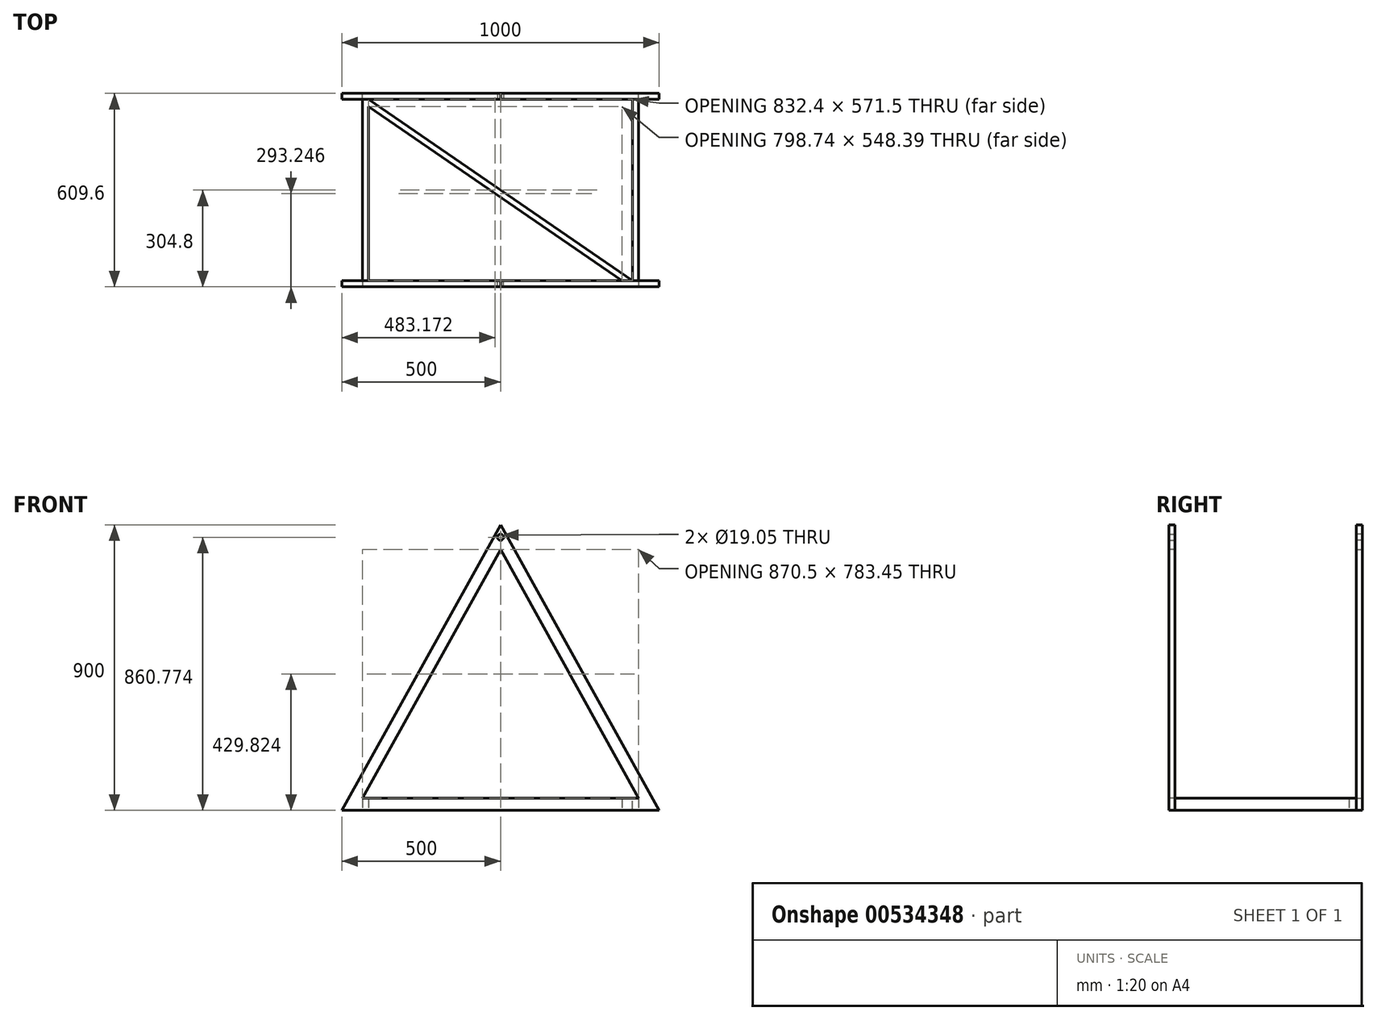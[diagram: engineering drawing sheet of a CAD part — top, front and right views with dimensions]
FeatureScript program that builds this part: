
annotation { "Feature Type Name" : "Feature", "Feature Type Description" : "" }
export const myFeature = defineFeature(function(context is Context, id is Id, definition is map)
    precondition{}
    {
        {
            var Q0;
            Q0=qCreatedBy(makeId("Front.planeOp"),FACE);
            var sketch = newSketch(context, id + "F0", { "sketchPlane" : qUnion([Q0])});
            skLineSegment(sketch, "E0", {"start": v(0, 900) * mm, "end": v(-500, 0) * mm});
            skLineSegment(sketch, "E1", {"start": v(-500, 0) * mm, "end": v(500, 0) * mm});
            skLineSegment(sketch, "E2", {"start": v(500, 0) * mm, "end": v(0, 900) * mm});
            skLineSegment(sketch, "E3", {"start": v(0, 900) * mm, "end": v(0, 0) * mm, "construction": true});
            skLineSegment(sketch, "E4", {"start": v(-478.83, 38.1) * mm, "end": v(478.83, 38.1) * mm});
            skLineSegment(sketch, "E5", {"start": v(-21.8, 860.77) * mm, "end": v(456.42, 0) * mm});
            skLineSegment(sketch, "E6", {"start": v(21.8, 860.77) * mm, "end": v(-456.42, 0) * mm});
            skSolve(sketch);
        }
        {
            var Q0;
            {var subQ0=sQuery(id+"F0.wireOp",EDGE,"E5");var subQ1=sQuery(id+"F0.wireOp",EDGE,"E1");var subQ2=makeQuery(id+"F0.imprint","INTERSECT",VERTEX,{"derivedFrom":[subQ1,subQ0]});Q0=makeQuery(id+"F0.imprint","IMPRINT",FACE,{"disambiguationData":[TD([[makeQuery(id+"F0.imprint","IMPRINT",EDGE,{"disambiguationData":[TD([[subQ2,1.0]])],"derivedFrom":subQ1}),1.0]])]});}
            extrude(context, id + "F1", {"entities" : qUnion([Q0]), "depth" : 19.05 * mm, "offsetDistance" : 25 * mm});
        }
        {
            var Q0;
            {var subQ0=sQuery(id+"F0.wireOp",EDGE,"E2");var subQ1=sQuery(id+"F0.wireOp",EDGE,"E1");var subQ2=makeQuery(id+"F0.imprint","INTERSECT",VERTEX,{"derivedFrom":[subQ1,subQ0]});Q0=makeQuery(id+"F0.imprint","IMPRINT",FACE,{"disambiguationData":[TD([[makeQuery(id+"F0.imprint","IMPRINT",EDGE,{"disambiguationData":[TD([[subQ2,1.0]])],"derivedFrom":subQ1}),1.0]])]});}
            var Q1;
            {var subQ0=sQuery(id+"F0.wireOp",EDGE,"E4");var subQ1=sQuery(id+"F0.wireOp",EDGE,"E2");var subQ2=makeQuery(id+"F0.imprint","INTERSECT",VERTEX,{"derivedFrom":[subQ1,subQ0]});Q1=makeQuery(id+"F0.imprint","IMPRINT",FACE,{"disambiguationData":[TD([[makeQuery(id+"F0.imprint","IMPRINT",EDGE,{"disambiguationData":[TD([[subQ2,-1.0]])],"derivedFrom":subQ1}),1.0]])]});}
            var Q2;
            {var subQ0=sQuery(id+"F0.wireOp",EDGE,"E2");var subQ1=sQuery(id+"F0.wireOp",EDGE,"E0");var subQ2=makeQuery(id+"F0.imprint","INTERSECT",VERTEX,{"derivedFrom":[subQ1,subQ0]});Q2=makeQuery(id+"F0.imprint","IMPRINT",FACE,{"disambiguationData":[TD([[makeQuery(id+"F0.imprint","IMPRINT",EDGE,{"disambiguationData":[TD([[subQ2,-1.0]])],"derivedFrom":subQ1}),1.0]])]});}
            var Q3;
            {var subQ0=sQuery(id+"F0.wireOp",EDGE,"E4");var subQ1=sQuery(id+"F0.wireOp",EDGE,"E0");var subQ2=makeQuery(id+"F0.imprint","INTERSECT",VERTEX,{"derivedFrom":[subQ1,subQ0]});Q3=makeQuery(id+"F0.imprint","IMPRINT",FACE,{"disambiguationData":[TD([[makeQuery(id+"F0.imprint","IMPRINT",EDGE,{"disambiguationData":[TD([[subQ2,1.0]])],"derivedFrom":subQ1}),1.0]])]});}
            var Q4;
            {var subQ0=sQuery(id+"F0.wireOp",EDGE,"E1");var subQ1=sQuery(id+"F0.wireOp",EDGE,"E0");var subQ2=makeQuery(id+"F0.imprint","INTERSECT",VERTEX,{"derivedFrom":[subQ1,subQ0]});Q4=makeQuery(id+"F0.imprint","IMPRINT",FACE,{"disambiguationData":[TD([[makeQuery(id+"F0.imprint","IMPRINT",EDGE,{"disambiguationData":[TD([[subQ2,1.0]])],"derivedFrom":subQ1}),1.0]])]});}
            extrude(context, id + "F2", {"entities" : qUnion([Q0, Q1, Q2, Q3, Q4]), "operationType" : NewBodyOperationType.ADD, "depth" : 19.05 * mm, "offsetDistance" : 25 * mm});
        }
        {
            var Q0;
            {var subQ0=sQuery(id+"F0.wireOp",EDGE,"E6");var subQ1=sQuery(id+"F0.wireOp",EDGE,"E5");var subQ2=sQuery(id+"F0.wireOp",EDGE,"E1");Q0=makeQuery(id+"F2.boolean.opBoolean","MERGE",FACE,{"derivedFrom":[makeQuery(id+"F1.opExtrude","CAP_FACE",FACE,{"disambiguationData":[OSD([subQ2,sQuery(id+"F0.wireOp",EDGE,"E4"),subQ1,subQ0])],"isStart":false}),makeQuery(id+"F2.opExtrude","CAP_FACE",FACE,{"disambiguationData":[OSD([sQuery(id+"F0.wireOp",EDGE,"E0"),subQ2,sQuery(id+"F0.wireOp",EDGE,"E2"),subQ1,subQ0])],"isStart":false})]});}
            var sketch = newSketch(context, id + "F3", { "sketchPlane" : qUnion([Q0])});
            skLineSegment(sketch, "E7", {"start": v(0, 900) * mm, "end": v(0, 821.55) * mm, "construction": true});
            skCircle(sketch, "E8", {"center": v(0, 860.77) * mm, "radius": 9.53 * mm});
            skSolve(sketch);
        }
        {
            var Q0;
            Q0=makeQuery(id+"F3.imprint","IMPRINT",FACE,{"disambiguationData":[TD([[makeQuery(id+"F3.imprint","IMPRINT",EDGE,{"derivedFrom":sQuery(id+"F3.wireOp",EDGE,"E8")}),1.0]])]});
            extrude(context, id + "F4", {"entities" : qUnion([Q0]), "operationType" : NewBodyOperationType.REMOVE, "oppositeDirection" : true, "depth" : 25 * mm, "offsetDistance" : 25 * mm});
        }
        {
            var Q0;
            {var subQ0=sQuery(id+"F0.wireOp",EDGE,"E6");var subQ1=sQuery(id+"F0.wireOp",EDGE,"E5");var subQ2=sQuery(id+"F0.wireOp",EDGE,"E1");Q0=makeQuery(id+"F2.boolean.opBoolean","MERGE",FACE,{"derivedFrom":[makeQuery(id+"F1.opExtrude","CAP_FACE",FACE,{"disambiguationData":[OSD([subQ2,sQuery(id+"F0.wireOp",EDGE,"E4"),subQ1,subQ0])],"isStart":false}),makeQuery(id+"F2.opExtrude","CAP_FACE",FACE,{"disambiguationData":[OSD([sQuery(id+"F0.wireOp",EDGE,"E0"),subQ2,sQuery(id+"F0.wireOp",EDGE,"E2"),subQ1,subQ0])],"isStart":false})]});}
            var sketch = newSketch(context, id + "F5", { "sketchPlane" : qUnion([Q0])});
            skLineSegment(sketch, "E9", {"start": v(-435.25, 38.1) * mm, "end": v(-435.25, 0) * mm});
            skLineSegment(sketch, "E10", {"start": v(-435.25, 0) * mm, "end": v(-416.2, 0) * mm});
            skLineSegment(sketch, "E11", {"start": v(-416.2, 0) * mm, "end": v(-416.2, 38.1) * mm});
            skLineSegment(sketch, "E12", {"start": v(-416.2, 38.1) * mm, "end": v(-435.25, 38.1) * mm});
            skLineSegment(sketch, "E13", {"start": v(435.25, 38.1) * mm, "end": v(435.25, 0) * mm});
            skLineSegment(sketch, "E14", {"start": v(435.25, 0) * mm, "end": v(416.2, 0) * mm});
            skLineSegment(sketch, "E15", {"start": v(416.2, 0) * mm, "end": v(416.2, 38.1) * mm});
            skLineSegment(sketch, "E16", {"start": v(416.2, 38.1) * mm, "end": v(435.25, 38.1) * mm});
            skSolve(sketch);
        }
        {
            var Q0;
            Q0=makeQuery(id+"F5.imprint","IMPRINT",FACE,{"disambiguationData":[TD([[makeQuery(id+"F5.imprint","IMPRINT",EDGE,{"derivedFrom":sQuery(id+"F5.wireOp",EDGE,"fFyfrfPh-Eq2j-K1ku-OToW-O3K3zpw26YUa")}),1.0]])]});
            var Q1;
            Q1=makeQuery(id+"F5.imprint","IMPRINT",FACE,{"disambiguationData":[TD([[makeQuery(id+"F5.imprint","IMPRINT",EDGE,{"derivedFrom":sQuery(id+"F5.wireOp",EDGE,"udyJFOjD-FLFl-QIxw-vqOu-JMlUizLs7YAt")}),-1.0]])]});
            var Q2;
            Q2=makeQuery(id+"F5.imprint","IMPRINT",FACE,{"disambiguationData":[TD([[makeQuery(id+"F5.imprint","IMPRINT",EDGE,{"derivedFrom":sQuery(id+"F5.wireOp",EDGE,"E9")}),1.0]])]});
            var Q3;
            Q3=makeQuery(id+"F5.imprint","IMPRINT",FACE,{"disambiguationData":[TD([[makeQuery(id+"F5.imprint","IMPRINT",EDGE,{"derivedFrom":sQuery(id+"F5.wireOp",EDGE,"E13")}),-1.0]])]});
            extrude(context, id + "F6", {"entities" : qUnion([Q0, Q1, Q2, Q3]), "operationType" : NewBodyOperationType.ADD, "depth" : (609.6 / 2 - 19.05) * mm, "offsetDistance" : 25 * mm});
        }
        {
            var Q0;
            Q0=makeQuery(id+"F1.opExtrude","SWEPT_BODY",BODY,{"disambiguationData":[OSD([sQuery(id+"F0.wireOp",EDGE,"E1"),sQuery(id+"F0.wireOp",EDGE,"E4"),sQuery(id+"F0.wireOp",EDGE,"E5"),sQuery(id+"F0.wireOp",EDGE,"E6")])]});
            var Q1;
            Q1=makeQuery(id+"F6.opExtrude","CAP_FACE",FACE,{"disambiguationData":[OSD([sQuery(id+"F5.wireOp",EDGE,"E13"),sQuery(id+"F5.wireOp",EDGE,"E14"),sQuery(id+"F5.wireOp",EDGE,"E15"),sQuery(id+"F5.wireOp",EDGE,"E16")])],"isStart":false});
            mirror(context, id + "F7", {"operationType" : NewBodyOperationType.ADD, "entities" : qUnion([Q0]), "mirrorPlane" : qUnion([Q1])});
        }
        {
            var Q0;
            Q0=qCreatedBy(makeId("Top.planeOp"),FACE);
            var sketch = newSketch(context, id + "F8", { "sketchPlane" : qUnion([Q0])});
            skLineSegment(sketch, "E17", {"start": v(-416.2, -19.05) * mm, "end": v(-416.2, -42.16) * mm});
            skLineSegment(sketch, "E18", {"start": v(-416.2, -42.16) * mm, "end": v(382.54, -590.55) * mm});
            skLineSegment(sketch, "E19", {"start": v(382.54, -590.55) * mm, "end": v(416.2, -590.55) * mm});
            skLineSegment(sketch, "E20", {"start": v(416.2, -590.55) * mm, "end": v(-416.2, -19.05) * mm});
            skLineSegment(sketch, "E21.0", {"start": v(-416.2, -590.55) * mm, "end": v(416.2, -590.55) * mm, "construction": true});
            skLineSegment(sketch, "E21.1", {"start": v(-416.2, -19.05) * mm, "end": v(416.2, -19.05) * mm, "construction": true});
            skSolve(sketch);
        }
        {
            var Q0;
            Q0=makeQuery(id+"F8.imprint","IMPRINT",FACE,{"disambiguationData":[TD([[makeQuery(id+"F8.imprint","IMPRINT",EDGE,{"derivedFrom":sQuery(id+"F8.wireOp",EDGE,"E17")}),1.0]])]});
            var Q1;
            {var subQ0=makeQuery(id+"F6.boolean.opBoolean","MERGE",FACE,{"derivedFrom":[makeQuery(id+"F1.opExtrude","SWEPT_FACE",FACE,{"disambiguationData":[OSD([sQuery(id+"F0.wireOp",EDGE,"E4")])]}),makeQuery(id+"F6.opExtrude","SWEPT_FACE",FACE,{"disambiguationData":[OSD([sQuery(id+"F5.wireOp",EDGE,"E12")])]}),makeQuery(id+"F6.opExtrude","SWEPT_FACE",FACE,{"disambiguationData":[OSD([sQuery(id+"F5.wireOp",EDGE,"E16")])]})]});Q1=makeQuery(id+"F7.boolean.opBoolean","MERGE",FACE,{"derivedFrom":[subQ0,makeQuery(id+"F7.opPattern","COPY",FACE,{"derivedFrom":subQ0,"instanceName":"1"})]});}
            extrude(context, id + "F9", {"entities" : qUnion([Q0]), "operationType" : NewBodyOperationType.ADD, "endBound" : BoundingType.UP_TO_SURFACE, "depth" : 25 * mm, "endBoundEntityFace" : qUnion([Q1]), "offsetDistance" : 25 * mm});
        }
    });
